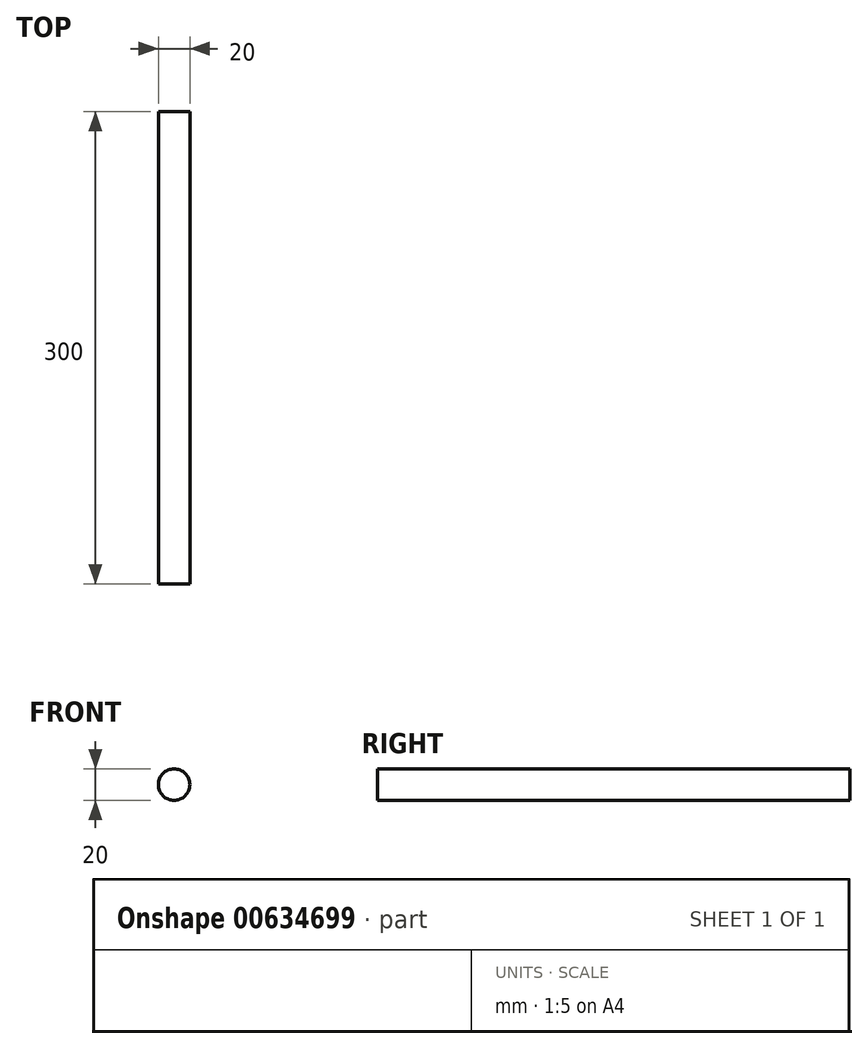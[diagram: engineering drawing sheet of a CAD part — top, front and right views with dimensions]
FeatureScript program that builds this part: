
annotation { "Feature Type Name" : "Feature", "Feature Type Description" : "" }
export const myFeature = defineFeature(function(context is Context, id is Id, definition is map)
    precondition{}
    {
        {
            var Q0;
            Q0=qCreatedBy(makeId("Front.planeOp"),FACE);
            var sketch = newSketch(context, id + "F0", { "sketchPlane" : qUnion([Q0])});
            skCircle(sketch, "E0", {"center": v(0, 0) * mm, "radius": 10 * mm});
            skSolve(sketch);
        }
        {
            var Q0;
            Q0 = qSketchRegion(id + "F0", true);
            extrude(context, id + "F1", {"entities" : qUnion([Q0]), "depth" : 300 * mm, "offsetDistance" : 25 * mm});
        }
    });
